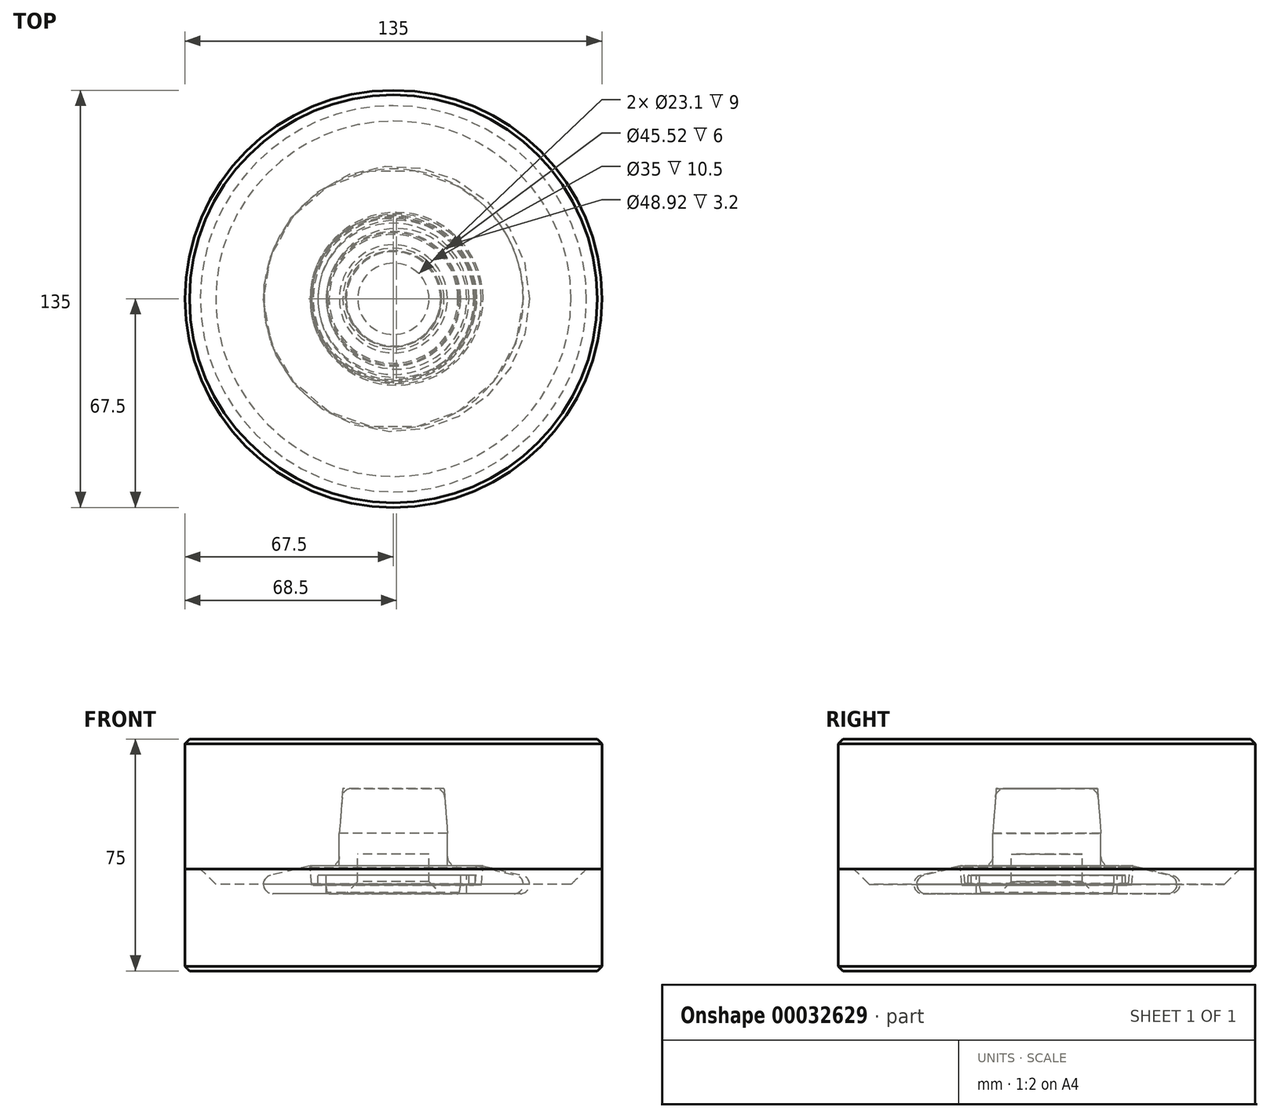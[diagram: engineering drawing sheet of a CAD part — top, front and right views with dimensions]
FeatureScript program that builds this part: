
annotation { "Feature Type Name" : "Feature", "Feature Type Description" : "" }
export const myFeature = defineFeature(function(context is Context, id is Id, definition is map)
    precondition{}
    {
        {
            var Q0;
            Q0=qCreatedBy(makeId("Front.planeOp"),FACE);
            var sketch = newSketch(context, id + "F0", { "sketchPlane" : qUnion([Q0])});
            skLineSegment(sketch, "E0", {"start": v(0, 46.51) * mm, "end": v(0, -43.52) * mm, "construction": true});
            skLineSegment(sketch, "E1", {"start": v(-17.5, 0) * mm, "end": v(-17.5, 10.5) * mm});
            skLineSegment(sketch, "E2", {"start": v(-16.4, 25) * mm, "end": v(16.4, 25) * mm});
            skLineSegment(sketch, "E3", {"start": v(-17.5, 0) * mm, "end": v(-27, 0) * mm});
            skLineSegment(sketch, "E4", {"start": v(-27, 0) * mm, "end": v(-26.46, -6.2) * mm});
            skLineSegment(sketch, "E5", {"start": v(-26.46, -6.2) * mm, "end": v(-24.46, -6.2) * mm});
            skLineSegment(sketch, "E6", {"start": v(-24.46, -6.2) * mm, "end": v(-24.46, -3) * mm});
            skLineSegment(sketch, "E7", {"start": v(-24.46, -3) * mm, "end": v(-21.76, -3) * mm});
            skLineSegment(sketch, "E8", {"start": v(-21.76, -3) * mm, "end": v(-21.76, -6.2) * mm});
            skLineSegment(sketch, "E9", {"start": v(-21.76, -6.2) * mm, "end": v(-21.26, -9) * mm});
            skLineSegment(sketch, "E10", {"start": v(-21.26, -9) * mm, "end": v(-15.4, -9) * mm});
            skLineSegment(sketch, "E11", {"start": v(-15.4, -9) * mm, "end": v(-11.55, -5.14) * mm});
            skLineSegment(sketch, "E12", {"start": v(-11.55, -5.14) * mm, "end": v(-11.55, 3.86) * mm});
            skLineSegment(sketch, "E13", {"start": v(-11.55, 3.86) * mm, "end": v(0, 3.86) * mm});
            skLineSegment(sketch, "E14.MirrorCS", {"start": v(21.76, -6.2) * mm, "end": v(21.26, -9) * mm});
            skLineSegment(sketch, "E15.MirrorCS", {"start": v(15.4, -9) * mm, "end": v(11.55, -5.14) * mm});
            skLineSegment(sketch, "E16.MirrorCS", {"start": v(21.26, -9) * mm, "end": v(15.4, -9) * mm});
            skLineSegment(sketch, "E17.MirrorCS", {"start": v(24.46, -6.2) * mm, "end": v(24.46, -3) * mm});
            skLineSegment(sketch, "E18.MirrorCS", {"start": v(24.46, -3) * mm, "end": v(21.76, -3) * mm});
            skLineSegment(sketch, "E19.MirrorCS", {"start": v(21.76, -3) * mm, "end": v(21.76, -6.2) * mm});
            skLineSegment(sketch, "E20.MirrorCS", {"start": v(26.46, -6.2) * mm, "end": v(24.46, -6.2) * mm});
            skLineSegment(sketch, "E21.MirrorCS", {"start": v(17.5, 0) * mm, "end": v(17.5, 10.5) * mm});
            skLineSegment(sketch, "E22.MirrorCS", {"start": v(27, 0) * mm, "end": v(26.46, -6.2) * mm});
            skLineSegment(sketch, "E23.MirrorCS", {"start": v(17.5, 0) * mm, "end": v(27, 0) * mm});
            skLineSegment(sketch, "E24.MirrorCS", {"start": v(11.55, 3.86) * mm, "end": v(0, 3.86) * mm});
            skLineSegment(sketch, "E25.MirrorCS", {"start": v(11.55, -5.14) * mm, "end": v(11.55, 3.86) * mm});
            skLineSegment(sketch, "E26", {"start": v(-22.87, 10.5) * mm, "end": v(21.36, 10.5) * mm, "construction": true});
            skLineSegment(sketch, "E27", {"start": v(-17.5, 10.5) * mm, "end": v(-16.4, 25) * mm});
            skLineSegment(sketch, "E28", {"start": v(17.5, 10.5) * mm, "end": v(16.4, 25) * mm});
            skLineSegment(sketch, "E29", {"start": v(0, 25) * mm, "end": v(0, 3.86) * mm});
            skLineSegment(sketch, "E30", {"start": v(-39.06, -9) * mm, "end": v(-21.76, -9) * mm});
            skLineSegment(sketch, "E31", {"start": v(-21.76, -6.2) * mm, "end": v(-21.76, -9) * mm});
            skCircle(sketch, "E32", {"center": v(-39.06, -6) * mm, "radius": 3 * mm});
            skLineSegment(sketch, "E33", {"start": v(1, -0.82) * mm, "end": v(1, -9.82) * mm, "construction": true});
            skLineSegment(sketch, "E34", {"start": v(-39.76, -3.08) * mm, "end": v(-27, 0) * mm});
            skLineSegment(sketch, "E35", {"start": v(-21.76, -9) * mm, "end": v(-21.26, -9) * mm});
            skLineSegment(sketch, "E36", {"start": v(-67.5, -9) * mm, "end": v(-67.5, 41) * mm});
            skLineSegment(sketch, "E37", {"start": v(-67.5, 41) * mm, "end": v(0, 41) * mm});
            skLineSegment(sketch, "E38", {"start": v(0, 41) * mm, "end": v(0, 25) * mm});
            skLineSegment(sketch, "E39", {"start": v(-67.5, -9) * mm, "end": v(-67.5, -34) * mm});
            skLineSegment(sketch, "E40", {"start": v(-67.5, -34) * mm, "end": v(0, -34) * mm});
            skLineSegment(sketch, "E41", {"start": v(0, -34) * mm, "end": v(0, 3.86) * mm});
            skLineSegment(sketch, "E42", {"start": v(-42.06, -6) * mm, "end": v(-67.5, -6) * mm});
            skLineSegment(sketch, "E43", {"start": v(-67.5, -1) * mm, "end": v(-62.5, -1) * mm});
            skLineSegment(sketch, "E44", {"start": v(-62.5, -1) * mm, "end": v(-57.5, -6) * mm});
            skSolve(sketch);
        }
        {
            var Q0;
            Q0=makeQuery(id+"F0.imprint","IMPRINT",FACE,{"disambiguationData":[TD([[makeQuery(id+"F0.imprint","IMPRINT",EDGE,{"derivedFrom":sQuery(id+"F0.wireOp",EDGE,"E1")}),-1.0]])]});
            var Q1;
            Q1=sQuery(id+"F0.wireOp",EDGE,"E29");
            revolve(context, id + "F1", {"entities" : qUnion([Q0]), "axis" : qUnion([Q1]), "revolveType" : RevolveType.FULL});
        }
        {
            var Q0;
            Q0=makeQuery(id+"F1.opRevolve","SWEPT_EDGE",EDGE,{"disambiguationData":[OSD([sQuery(id+"F0.wireOp",EDGE,"E2"),sQuery(id+"F0.wireOp",EDGE,"E27")])]});
            fillet(context, id + "F2", {"entities" : qUnion([Q0]), "radius" : 3 * mm, "tangentPropagation" : true, "allowEdgeOverflow" : false});
        }
        {
            var Q0;
            Q0=makeQuery(id+"F1.opRevolve","SWEPT_EDGE",EDGE,{"disambiguationData":[OSD([sQuery(id+"F0.wireOp",EDGE,"E1"),sQuery(id+"F0.wireOp",EDGE,"E3")])]});
            fillet(context, id + "F3", {"entities" : qUnion([Q0]), "radius" : 3 * mm, "tangentPropagation" : true, "allowEdgeOverflow" : false});
        }
        {
            var Q0;
            Q0=makeQuery(id+"F1.opRevolve","SWEPT_EDGE",EDGE,{"disambiguationData":[OSD([sQuery(id+"F0.wireOp",EDGE,"E3"),sQuery(id+"F0.wireOp",EDGE,"E4")])]});
            var Q1;
            Q1=makeQuery(id+"F1.opRevolve","SWEPT_EDGE",EDGE,{"disambiguationData":[OSD([sQuery(id+"F0.wireOp",EDGE,"E4"),sQuery(id+"F0.wireOp",EDGE,"E5")])]});
            var Q2;
            Q2=makeQuery(id+"F1.opRevolve","SWEPT_EDGE",EDGE,{"disambiguationData":[OSD([sQuery(id+"F0.wireOp",EDGE,"E9"),sQuery(id+"F0.wireOp",EDGE,"E10")])]});
            var Q3;
            Q3=makeQuery(id+"F1.opRevolve","SWEPT_EDGE",EDGE,{"disambiguationData":[OSD([sQuery(id+"F0.wireOp",EDGE,"E10"),sQuery(id+"F0.wireOp",EDGE,"E11")])]});
            chamfer(context, id + "F4", {"entities" : qUnion([Q0, Q1, Q2, Q3]), "width" : .5 * mm, "tangentPropagation" : true});
        }
        {
            var Q0;
            {var subQ3=sQuery(id+"F0.wireOp",EDGE,"E4");Q0=makeQuery(id+"F0.imprint","IMPRINT",FACE,{"disambiguationData":[TD([[makeQuery(id+"F0.imprint","IMPRINT",EDGE,{"derivedFrom":subQ3}),-1.0]])]});}
            var Q1;
            {var subQ0=sQuery(id+"F0.wireOp",EDGE,"E32");var subQ1=sQuery(id+"F0.wireOp",EDGE,"1cee8f10-8f5e-4a27-858d-b2fedd833254");var subQ2=makeQuery(id+"F0.imprint","INTERSECT",VERTEX,{"derivedFrom":[subQ1,subQ0]});Q1=makeQuery(id+"F0.imprint","IMPRINT",FACE,{"disambiguationData":[TD([[makeQuery(id+"F0.imprint","IMPRINT",EDGE,{"disambiguationData":[TD([[subQ2,-1.0]])],"derivedFrom":subQ1}),1.0]])]});}
            var Q2;
            {var subQ0=sQuery(id+"F0.wireOp",EDGE,"E32");var subQ5=makeQuery(id+"F0.imprint","INTERSECT",VERTEX,{"derivedFrom":[subQ0,sQuery(id+"F0.wireOp",EDGE,"21bd987d-5c50-46d4-8a6c-0cccb9aafa64")]});Q2=makeQuery(id+"F0.imprint","IMPRINT",FACE,{"disambiguationData":[TD([[makeQuery(id+"F0.imprint","IMPRINT",EDGE,{"disambiguationData":[TD([[subQ5,1.0]])],"derivedFrom":subQ0}),1.0]])]});}
            var Q3;
            Q3=sQuery(id+"F0.wireOp",EDGE,"E33");
            revolve(context, id + "F5", {"entities" : qUnion([Q0, Q1, Q2]), "axis" : qUnion([Q3]), "revolveType" : RevolveType.FULL});
        }
        {
            var Q0;
            Q0=makeQuery(id+"F0.imprint","IMPRINT",FACE,{"disambiguationData":[TD([[makeQuery(id+"F0.imprint","IMPRINT",EDGE,{"derivedFrom":sQuery(id+"F0.wireOp",EDGE,"E1")}),-1.0]])]});
            var Q1;
            Q1=makeQuery(id+"F0.imprint","IMPRINT",FACE,{"disambiguationData":[TD([[makeQuery(id+"F0.imprint","IMPRINT",EDGE,{"derivedFrom":sQuery(id+"F0.wireOp",EDGE,"E4")}),-1.0]])]});
            var Q2;
            {var subQ0=sQuery(id+"F0.wireOp",EDGE,"E32");var subQ1=makeQuery(id+"F0.imprint","INTERSECT",VERTEX,{"derivedFrom":[sQuery(id+"F0.wireOp",EDGE,"E30"),subQ0]});Q2=makeQuery(id+"F0.imprint","IMPRINT",FACE,{"disambiguationData":[TD([[makeQuery(id+"F0.imprint","IMPRINT",EDGE,{"disambiguationData":[TD([[subQ1,1.0]])],"derivedFrom":subQ0}),1.0]])]});}
            var Q3;
            Q3=makeQuery(id+"F0.imprint","IMPRINT",FACE,{"disambiguationData":[TD([[makeQuery(id+"F0.imprint","IMPRINT",EDGE,{"derivedFrom":sQuery(id+"F0.wireOp",EDGE,"E9")}),-1.0]])]});
            var Q4;
            Q4=sQuery(id+"F0.wireOp",EDGE,"E0");
            revolve(context, id + "F6", {"entities" : qUnion([Q0, Q1, Q2, Q3]), "axis" : qUnion([Q4]), "revolveType" : RevolveType.FULL});
        }
        {
            var Q0;
            Q0=makeQuery(id+"F0.imprint","IMPRINT",FACE,{"disambiguationData":[TD([[makeQuery(id+"F0.imprint","IMPRINT",EDGE,{"derivedFrom":sQuery(id+"F0.wireOp",EDGE,"E10")}),-1.0]])]});
            var Q1;
            {var subQ3=sQuery(id+"F0.wireOp",EDGE,"E43");Q1=makeQuery(id+"F0.imprint","IMPRINT",FACE,{"disambiguationData":[TD([[makeQuery(id+"F0.imprint","IMPRINT",EDGE,{"derivedFrom":subQ3}),-1.0]])]});}
            var Q2;
            Q2=sQuery(id+"F0.wireOp",EDGE,"E0");
            revolve(context, id + "F7", {"entities" : qUnion([Q0, Q1]), "axis" : qUnion([Q2]), "revolveType" : RevolveType.FULL});
        }
        {
            var Q0;
            Q0=makeQuery(id+"F0.imprint","IMPRINT",FACE,{"disambiguationData":[TD([[makeQuery(id+"F0.imprint","IMPRINT",EDGE,{"derivedFrom":sQuery(id+"F0.wireOp",EDGE,"E1")}),1.0]])]});
            var Q1;
            Q1=sQuery(id+"F0.wireOp",EDGE,"E0");
            revolve(context, id + "F8", {"entities" : qUnion([Q0]), "axis" : qUnion([Q1]), "revolveType" : RevolveType.FULL});
        }
        {
            var Q0;
            Q0=makeQuery(id+"F7.opRevolve","SWEPT_EDGE",EDGE,{"disambiguationData":[OSD([sQuery(id+"F0.wireOp",EDGE,"E39"),sQuery(id+"F0.wireOp",EDGE,"E40")])]});
            chamfer(context, id + "F9", {"entities" : qUnion([Q0]), "width" : 1.5 * mm, "tangentPropagation" : true});
        }
        {
            var Q0;
            Q0=makeQuery(id+"F8.opRevolve","SWEPT_EDGE",EDGE,{"disambiguationData":[OSD([sQuery(id+"F0.wireOp",EDGE,"E36"),sQuery(id+"F0.wireOp",EDGE,"E37")])]});
            chamfer(context, id + "F10", {"entities" : qUnion([Q0]), "width" : 1.5 * mm, "tangentPropagation" : true});
        }
    });
